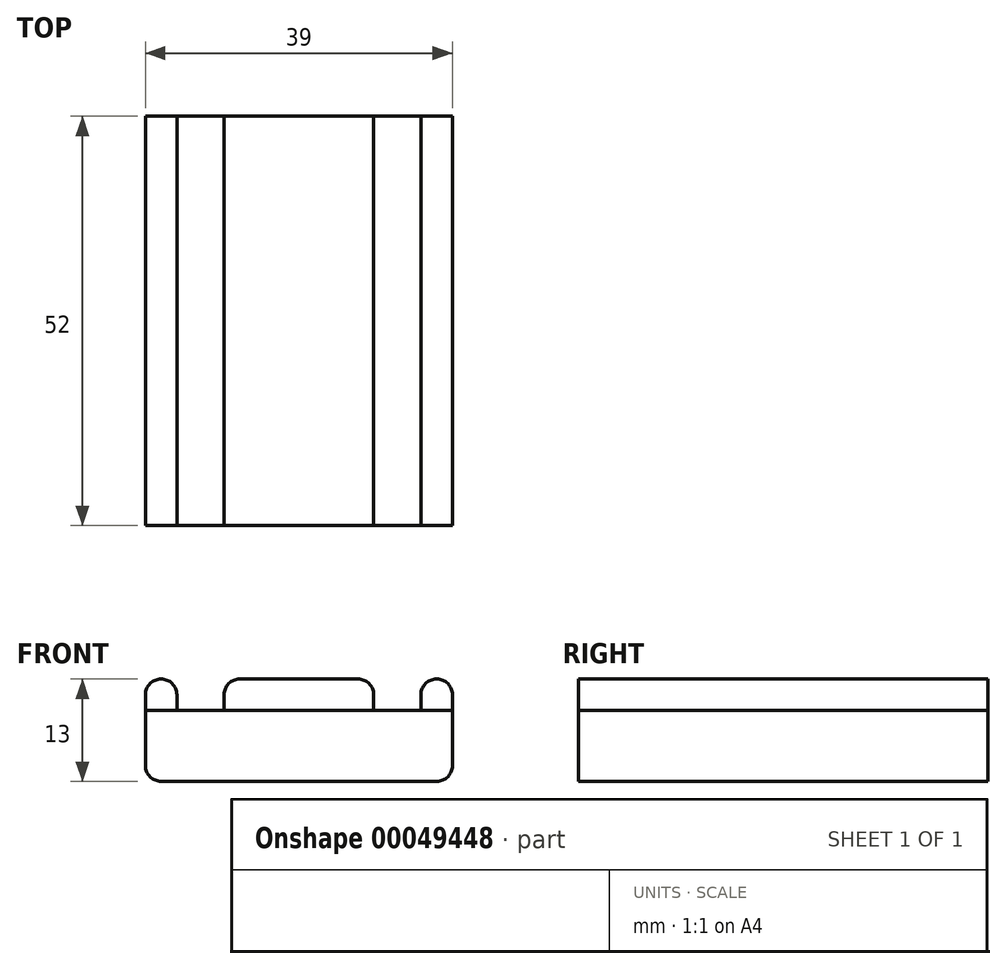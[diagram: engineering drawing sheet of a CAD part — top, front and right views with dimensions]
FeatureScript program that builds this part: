
annotation { "Feature Type Name" : "Feature", "Feature Type Description" : "" }
export const myFeature = defineFeature(function(context is Context, id is Id, definition is map)
    precondition{}
    {
        {
            var Q0;
            Q0=qCreatedBy(makeId("Top.planeOp"),FACE);
            var sketch = newSketch(context, id + "F0", { "sketchPlane" : qUnion([Q0])});
            skPoint(sketch, "E0", {"position": v(0, 26.15) * mm});
            skPoint(sketch, "E1", {"position": v(0, -25.85) * mm});
            skPoint(sketch, "E2", {"position": v(21.98, -25.85) * mm});
            skPoint(sketch, "E3", {"position": v(19.5, -25.85) * mm});
            skPoint(sketch, "E4", {"position": v(-24.92, 26.15) * mm});
            skPoint(sketch, "E5", {"position": v(-19.5, 26.15) * mm});
            skLineSegment(sketch, "E6.bottom", {"start": v(-19.5, 26.15) * mm, "end": v(19.5, 26.15) * mm});
            skLineSegment(sketch, "E6.top", {"start": v(-19.5, -25.85) * mm, "end": v(19.5, -25.85) * mm});
            skLineSegment(sketch, "E6.left", {"start": v(-19.5, 26.15) * mm, "end": v(-19.5, -25.85) * mm});
            skLineSegment(sketch, "E6.right", {"start": v(19.5, 26.15) * mm, "end": v(19.5, -25.85) * mm});
            skSolve(sketch);
        }
        {
            var Q0;
            Q0=makeQuery(id+"F0.imprint","IMPRINT",FACE,{"disambiguationData":[TD([[makeQuery(id+"F0.imprint","IMPRINT",EDGE,{"derivedFrom":sQuery(id+"F0.wireOp",EDGE,"E6.bottom")}),-1.0]])]});
            extrude(context, id + "F1", {"entities" : qUnion([Q0]), "depth" : 9 * mm});
        }
        {
            var Q0;
            Q0=makeQuery(id+"F1.opExtrude","CAP_FACE",FACE,{"disambiguationData":[OSD([sQuery(id+"F0.wireOp",EDGE,"E6.bottom"),sQuery(id+"F0.wireOp",EDGE,"E6.top"),sQuery(id+"F0.wireOp",EDGE,"E6.left"),sQuery(id+"F0.wireOp",EDGE,"E6.right")])],"isStart":false});
            var sketch = newSketch(context, id + "F2", { "sketchPlane" : qUnion([Q0])});
            skPoint(sketch, "E7", {"position": v(0, 26.15) * mm});
            skPoint(sketch, "E8", {"position": v(0, -25.85) * mm});
            skPoint(sketch, "E9", {"position": v(3.27, 26.15) * mm});
            skPoint(sketch, "E10", {"position": v(4, 26.15) * mm});
            skLineSegment(sketch, "E11.bottom", {"start": v(4, 26.15) * mm, "end": v(0, 26.15) * mm});
            skLineSegment(sketch, "E11.top", {"start": v(4, -25.85) * mm, "end": v(0, -25.85) * mm});
            skLineSegment(sketch, "E11.left", {"start": v(4, 26.15) * mm, "end": v(4, -25.85) * mm});
            skLineSegment(sketch, "E11.right", {"start": v(0, 26.15) * mm, "end": v(0, -25.85) * mm});
            skSolve(sketch);
        }
        {
            var Q0;
            Q0=makeQuery(id+"F2.imprint","IMPRINT",FACE,{"disambiguationData":[TD([[makeQuery(id+"F2.imprint","IMPRINT",EDGE,{"derivedFrom":sQuery(id+"F2.wireOp",EDGE,"E11.bottom")}),-1.0]])]});
            extrude(context, id + "F3", {"entities" : qUnion([Q0]), "depth" : 4 * mm});
        }
        {
            var Q0;
            Q0=makeQuery(id+"F3.opExtrude","SWEPT_BODY",BODY,{"disambiguationData":[OSD([sQuery(id+"F2.wireOp",EDGE,"E11.bottom"),sQuery(id+"F2.wireOp",EDGE,"E11.top"),sQuery(id+"F2.wireOp",EDGE,"E11.left"),sQuery(id+"F2.wireOp",EDGE,"E11.right")])]});
            transform(context, id + "F4", {"entities" : qUnion([Q0]), "transformType" : TransformType.TRANSLATION_3D, "dx" : 15.5 * mm, "dy" : 0 * mm, "dz" : 0 * mm, "makeCopy" : false});
        }
        {
            var Q0;
            Q0=makeQuery(id+"F3.opExtrude","SWEPT_BODY",BODY,{"disambiguationData":[OSD([sQuery(id+"F2.wireOp",EDGE,"E11.bottom"),sQuery(id+"F2.wireOp",EDGE,"E11.top"),sQuery(id+"F2.wireOp",EDGE,"E11.left"),sQuery(id+"F2.wireOp",EDGE,"E11.right")])]});
            transform(context, id + "F5", {"entities" : qUnion([Q0]), "transformType" : TransformType.TRANSLATION_3D, "dx" : -35 * mm, "dy" : 0 * mm, "dz" : 0 * mm, "makeCopy" : true});
        }
        {
            var Q0;
            Q0=makeQuery(id+"F1.opExtrude","CAP_FACE",FACE,{"disambiguationData":[OSD([sQuery(id+"F0.wireOp",EDGE,"E6.bottom"),sQuery(id+"F0.wireOp",EDGE,"E6.top"),sQuery(id+"F0.wireOp",EDGE,"E6.left"),sQuery(id+"F0.wireOp",EDGE,"E6.right")])],"isStart":false});
            var sketch = newSketch(context, id + "F6", { "sketchPlane" : qUnion([Q0])});
            skPoint(sketch, "E12", {"position": v(0, 26.15) * mm});
            skPoint(sketch, "E13", {"position": v(0, -25.85) * mm});
            skPoint(sketch, "E14", {"position": v(33.42, -7.56) * mm});
            skPoint(sketch, "E15", {"position": v(9.5, 26.15) * mm});
            skPoint(sketch, "E16", {"position": v(-5.4, -25.85) * mm});
            skPoint(sketch, "E17", {"position": v(-9.5, -25.85) * mm});
            skLineSegment(sketch, "E18.bottom", {"start": v(-9.5, -25.85) * mm, "end": v(9.5, -25.85) * mm});
            skLineSegment(sketch, "E18.top", {"start": v(-9.5, 26.15) * mm, "end": v(9.5, 26.15) * mm});
            skLineSegment(sketch, "E18.left", {"start": v(-9.5, -25.85) * mm, "end": v(-9.5, 26.15) * mm});
            skLineSegment(sketch, "E18.right", {"start": v(9.5, -25.85) * mm, "end": v(9.5, 26.15) * mm});
            skSolve(sketch);
        }
        {
            var Q0;
            Q0=makeQuery(id+"F6.imprint","IMPRINT",FACE,{"disambiguationData":[TD([[makeQuery(id+"F6.imprint","IMPRINT",EDGE,{"derivedFrom":sQuery(id+"F6.wireOp",EDGE,"E18.bottom")}),1.0]])]});
            extrude(context, id + "F7", {"entities" : qUnion([Q0]), "depth" : 4 * mm});
        }
        {
            var Q0;
            Q0=makeQuery(id+"F5.opPattern","COPY",EDGE,{"derivedFrom":makeQuery(id+"F3.opExtrude","CAP_EDGE",EDGE,{"disambiguationData":[OSD([sQuery(id+"F2.wireOp",EDGE,"E11.left")])],"isStart":false}),"instanceName":"1"});
            fillet(context, id + "F8", {"entities" : qUnion([Q0]), "radius" : 2 * mm, "tangentPropagation" : true, "allowEdgeOverflow" : false});
        }
        {
            var Q0;
            Q0=makeQuery(id+"F5.opPattern","COPY",EDGE,{"derivedFrom":makeQuery(id+"F3.opExtrude","CAP_EDGE",EDGE,{"disambiguationData":[OSD([sQuery(id+"F2.wireOp",EDGE,"E11.right")])],"isStart":false}),"instanceName":"1"});
            fillet(context, id + "F9", {"entities" : qUnion([Q0]), "radius" : 2 * mm, "tangentPropagation" : true, "allowEdgeOverflow" : false});
        }
        {
            var Q0;
            Q0=makeQuery(id+"F7.opExtrude","CAP_EDGE",EDGE,{"disambiguationData":[OSD([sQuery(id+"F6.wireOp",EDGE,"E18.left")])],"isStart":false});
            var Q1;
            Q1=makeQuery(id+"F7.opExtrude","CAP_EDGE",EDGE,{"disambiguationData":[OSD([sQuery(id+"F6.wireOp",EDGE,"E18.right")])],"isStart":false});
            var Q2;
            Q2=makeQuery(id+"F3.opExtrude","CAP_EDGE",EDGE,{"disambiguationData":[OSD([sQuery(id+"F2.wireOp",EDGE,"E11.right")])],"isStart":false});
            var Q3;
            Q3=makeQuery(id+"F3.opExtrude","CAP_EDGE",EDGE,{"disambiguationData":[OSD([sQuery(id+"F2.wireOp",EDGE,"E11.left")])],"isStart":false});
            var Q4;
            Q4=makeQuery(id+"F1.opExtrude","CAP_EDGE",EDGE,{"disambiguationData":[OSD([sQuery(id+"F0.wireOp",EDGE,"E6.right")])],"isStart":true});
            var Q5;
            Q5=makeQuery(id+"F1.opExtrude","CAP_EDGE",EDGE,{"disambiguationData":[OSD([sQuery(id+"F0.wireOp",EDGE,"E6.left")])],"isStart":true});
            fillet(context, id + "F10", {"entities" : qUnion([Q0, Q1, Q2, Q3, Q4, Q5]), "radius" : 2 * mm, "tangentPropagation" : true, "allowEdgeOverflow" : false});
        }
        {
            var Q0;
            Q0=qCreatedBy(makeId("Top.planeOp"),FACE);
            var sketch = newSketch(context, id + "F11", { "sketchPlane" : qUnion([Q0])});
            skPoint(sketch, "E19", {"position": v(4, 0) * mm});
            skPoint(sketch, "E20", {"position": v(-4, 0) * mm});
            skPoint(sketch, "E21", {"position": v(0, 33.11) * mm});
            skPoint(sketch, "E22", {"position": v(0, 35) * mm});
            skPoint(sketch, "E23", {"position": v(0, 0) * mm});
            skPoint(sketch, "E24", {"position": v(3.48, 35) * mm});
            skPoint(sketch, "E25", {"position": v(4, 35) * mm});
            skLineSegment(sketch, "E26.bottom", {"start": v(-4, 0) * mm, "end": v(4, 0) * mm});
            skLineSegment(sketch, "E26.top", {"start": v(-4, 35) * mm, "end": v(4, 35) * mm});
            skLineSegment(sketch, "E26.left", {"start": v(-4, 0) * mm, "end": v(-4, 35) * mm});
            skLineSegment(sketch, "E26.right", {"start": v(4, 0) * mm, "end": v(4, 35) * mm});
            skCircle(sketch, "E27", {"center": v(0, 0) * mm, "radius": 6.5 * mm});
            skSolve(sketch);
        }
        {
            var Q0;
            {var subQ5=sQuery(id+"F11.wireOp",EDGE,"E26.bottom");Q0=makeQuery(id+"F11.imprint","IMPRINT",FACE,{"disambiguationData":[TD([[makeQuery(id+"F11.imprint","IMPRINT",EDGE,{"derivedFrom":subQ5}),-1.0]])]});}
            var Q1;
            {var subQ5=sQuery(id+"F11.wireOp",EDGE,"E26.bottom");Q1=makeQuery(id+"F11.imprint","IMPRINT",FACE,{"disambiguationData":[TD([[makeQuery(id+"F11.imprint","IMPRINT",EDGE,{"derivedFrom":subQ5}),1.0]])]});}
            var Q2;
            {var subQ5=sQuery(id+"F11.wireOp",EDGE,"E26.top");Q2=makeQuery(id+"F11.imprint","IMPRINT",FACE,{"disambiguationData":[TD([[makeQuery(id+"F11.imprint","IMPRINT",EDGE,{"derivedFrom":subQ5}),-1.0]])]});}
            extrude(context, id + "F12", {"entities" : qUnion([Q0, Q1, Q2]), "depth" : 25 * mm, "hasSecondDirection" : true, "secondDirectionOppositeDirection" : true, "secondDirectionDepth" : 25 * mm});
        }
        {
            var Q0;
            Q0=makeQuery(id+"F12.opExtrude","SWEPT_BODY",BODY,{"disambiguationData":[OSD([sQuery(id+"F11.wireOp",EDGE,"E26.top"),sQuery(id+"F11.wireOp",EDGE,"E26.left"),sQuery(id+"F11.wireOp",EDGE,"E26.right"),sQuery(id+"F11.wireOp",EDGE,"E27")])]});
            transform(context, id + "F13", {"entities" : qUnion([Q0]), "transformType" : TransformType.TRANSLATION_3D, "dx" : 0 * mm, "dy" : 15 * mm, "dz" : 0 * mm, "makeCopy" : false});
        }
        {
            var Q0;
            Q0=qCreatedBy(makeId("Top.planeOp"),FACE);
            var sketch = newSketch(context, id + "F14", { "sketchPlane" : qUnion([Q0])});
            skLineSegment(sketch, "E28", {"start": v(-39.78, 0) * mm, "end": v(49.97, 0) * mm});
            skSolve(sketch);
        }
        {
            var Q0;
            Q0=makeQuery(id+"F12.opExtrude","SWEPT_BODY",BODY,{"disambiguationData":[OSD([sQuery(id+"F11.wireOp",EDGE,"E26.top"),sQuery(id+"F11.wireOp",EDGE,"E26.left"),sQuery(id+"F11.wireOp",EDGE,"E26.right"),sQuery(id+"F11.wireOp",EDGE,"E27")])]});
            var Q1;
            Q1=sQuery(id+"F14.wireOp",EDGE,"E28");
            transform(context, id + "F15", {"entities" : qUnion([Q0]), "transformType" : TransformType.ROTATION, "transformAxis" : qUnion([Q1]), "angle" : 180 * degree, "makeCopy" : true});
        }
        {
            var Q0;
            Q0=makeQuery(id+"F15.opPattern","COPY",BODY,{"derivedFrom":makeQuery(id+"F12.opExtrude","SWEPT_BODY",BODY,{"disambiguationData":[OSD([sQuery(id+"F11.wireOp",EDGE,"E26.top"),sQuery(id+"F11.wireOp",EDGE,"E26.left"),sQuery(id+"F11.wireOp",EDGE,"E26.right"),sQuery(id+"F11.wireOp",EDGE,"E27")])]}),"instanceName":"1"});
            var Q1;
            Q1=makeQuery(id+"F3.opExtrude","SWEPT_BODY",BODY,{"disambiguationData":[OSD([sQuery(id+"F2.wireOp",EDGE,"E11.bottom"),sQuery(id+"F2.wireOp",EDGE,"E11.top"),sQuery(id+"F2.wireOp",EDGE,"E11.left"),sQuery(id+"F2.wireOp",EDGE,"E11.right")])]});
            booleanBodies(context, id + "F16", {"operationType" : BooleanOperationType.SUBTRACTION, "tools" : qUnion([Q0]), "targets" : qUnion([Q1])});
        }
        {
            var Q0;
            Q0=makeQuery(id+"F12.opExtrude","SWEPT_BODY",BODY,{"disambiguationData":[OSD([sQuery(id+"F11.wireOp",EDGE,"E26.top"),sQuery(id+"F11.wireOp",EDGE,"E26.left"),sQuery(id+"F11.wireOp",EDGE,"E26.right"),sQuery(id+"F11.wireOp",EDGE,"E27")])]});
            var Q1;
            Q1=makeQuery(id+"F3.opExtrude","SWEPT_BODY",BODY,{"disambiguationData":[OSD([sQuery(id+"F2.wireOp",EDGE,"E11.bottom"),sQuery(id+"F2.wireOp",EDGE,"E11.top"),sQuery(id+"F2.wireOp",EDGE,"E11.left"),sQuery(id+"F2.wireOp",EDGE,"E11.right")])]});
            booleanBodies(context, id + "F17", {"operationType" : BooleanOperationType.SUBTRACTION, "tools" : qUnion([Q0]), "targets" : qUnion([Q1])});
        }
    });
